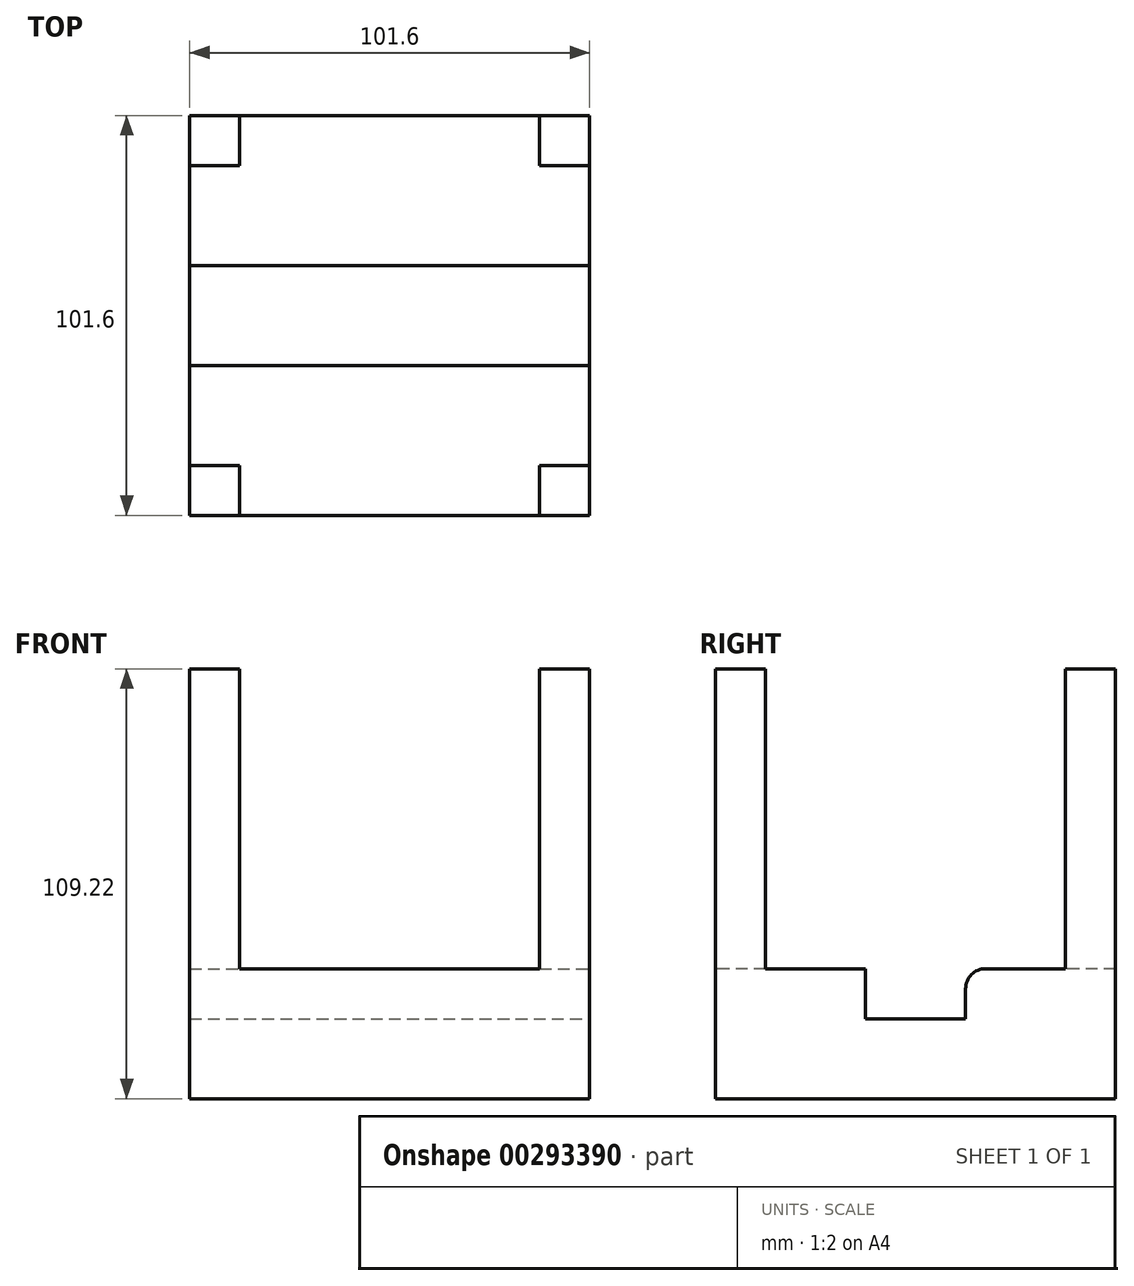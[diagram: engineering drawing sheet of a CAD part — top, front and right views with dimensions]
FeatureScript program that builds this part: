
annotation { "Feature Type Name" : "Feature", "Feature Type Description" : "" }
export const myFeature = defineFeature(function(context is Context, id is Id, definition is map)
    precondition{}
    {
        {
            var Q0;
            Q0=qCreatedBy(makeId("Top.planeOp"),FACE);
            var sketch = newSketch(context, id + "F0", { "sketchPlane" : qUnion([Q0])});
            skLineSegment(sketch, "E0.bottom", {"start": v(50.8, 50.8) * mm, "end": v(-50.8, 50.8) * mm});
            skLineSegment(sketch, "E0.top", {"start": v(50.8, -50.8) * mm, "end": v(-50.8, -50.8) * mm});
            skLineSegment(sketch, "E0.left", {"start": v(50.8, 50.8) * mm, "end": v(50.8, -50.8) * mm});
            skLineSegment(sketch, "E0.right", {"start": v(-50.8, 50.8) * mm, "end": v(-50.8, -50.8) * mm});
            skPoint(sketch, "E0.middle", {"position": v(0, 0) * mm});
            skSolve(sketch);
        }
        {
            var Q0;
            Q0=makeQuery(id+"F0.imprint","IMPRINT",FACE,{"disambiguationData":[TD([[makeQuery(id+"F0.imprint","IMPRINT",EDGE,{"derivedFrom":sQuery(id+"F0.wireOp",EDGE,"E0.bottom")}),1.0]])]});
            extrude(context, id + "F1", {"entities" : qUnion([Q0]), "depth" : 33.02 * mm});
        }
        {
            var Q0;
            Q0=makeQuery(id+"F1.opExtrude","CAP_FACE",FACE,{"disambiguationData":[OSD([sQuery(id+"F0.wireOp",EDGE,"E0.bottom"),sQuery(id+"F0.wireOp",EDGE,"E0.top"),sQuery(id+"F0.wireOp",EDGE,"E0.left"),sQuery(id+"F0.wireOp",EDGE,"E0.right")])],"isStart":false});
            var sketch = newSketch(context, id + "F2", { "sketchPlane" : qUnion([Q0])});
            skLineSegment(sketch, "E1", {"start": v(-50.8, 50.8) * mm, "end": v(-38.1, 50.8) * mm});
            skLineSegment(sketch, "E2", {"start": v(-38.1, 50.8) * mm, "end": v(-38.1, 38.1) * mm});
            skLineSegment(sketch, "E3", {"start": v(-38.1, 38.1) * mm, "end": v(-50.8, 38.1) * mm});
            skLineSegment(sketch, "E4", {"start": v(50.8, 50.8) * mm, "end": v(38.1, 50.8) * mm});
            skLineSegment(sketch, "E5", {"start": v(38.1, 50.8) * mm, "end": v(38.1, 38.1) * mm});
            skLineSegment(sketch, "E6", {"start": v(38.1, 38.1) * mm, "end": v(50.8, 38.1) * mm});
            skLineSegment(sketch, "E7", {"start": v(-50.8, -50.8) * mm, "end": v(-50.8, -38.1) * mm});
            skLineSegment(sketch, "E8", {"start": v(-50.8, -38.1) * mm, "end": v(-38.1, -38.1) * mm});
            skLineSegment(sketch, "E9", {"start": v(-38.1, -38.1) * mm, "end": v(-38.1, -50.8) * mm});
            skLineSegment(sketch, "E10", {"start": v(50.8, -50.8) * mm, "end": v(38.1, -50.8) * mm});
            skLineSegment(sketch, "E11", {"start": v(38.1, -50.8) * mm, "end": v(38.1, -38.1) * mm});
            skLineSegment(sketch, "E12", {"start": v(38.1, -38.1) * mm, "end": v(50.8, -38.1) * mm});
            skSolve(sketch);
        }
        {
            var Q0;
            {var subQ0=sQuery(id+"F2.wireOp",EDGE,"E10");Q0=makeQuery(id+"F2.imprint","IMPRINT",FACE,{"disambiguationData":[TD([[makeQuery(id+"F2.imprint","IMPRINT",EDGE,{"derivedFrom":subQ0}),-1.0]])]});}
            var Q1;
            {var subQ0=sQuery(id+"F2.wireOp",EDGE,"E7");Q1=makeQuery(id+"F2.imprint","IMPRINT",FACE,{"disambiguationData":[TD([[makeQuery(id+"F2.imprint","IMPRINT",EDGE,{"derivedFrom":subQ0}),1.0]])]});}
            var Q2;
            {var subQ0=sQuery(id+"F2.wireOp",EDGE,"E1");Q2=makeQuery(id+"F2.imprint","IMPRINT",FACE,{"disambiguationData":[TD([[makeQuery(id+"F2.imprint","IMPRINT",EDGE,{"derivedFrom":subQ0}),1.0]])]});}
            var Q3;
            {var subQ0=sQuery(id+"F2.wireOp",EDGE,"E4");Q3=makeQuery(id+"F2.imprint","IMPRINT",FACE,{"disambiguationData":[TD([[makeQuery(id+"F2.imprint","IMPRINT",EDGE,{"derivedFrom":subQ0}),1.0]])]});}
            extrude(context, id + "F3", {"entities" : qUnion([Q0, Q1, Q2, Q3]), "operationType" : NewBodyOperationType.ADD, "depth" : 76.2 * mm});
        }
        {
            var Q0;
            Q0=makeQuery(id+"F1.opExtrude","CAP_FACE",FACE,{"disambiguationData":[OSD([sQuery(id+"F0.wireOp",EDGE,"E0.bottom"),sQuery(id+"F0.wireOp",EDGE,"E0.top"),sQuery(id+"F0.wireOp",EDGE,"E0.left"),sQuery(id+"F0.wireOp",EDGE,"E0.right")])],"isStart":false});
            var sketch = newSketch(context, id + "F4", { "sketchPlane" : qUnion([Q0])});
            skLineSegment(sketch, "E13", {"start": v(-50.8, 38.1) * mm, "end": v(-50.8, 12.7) * mm});
            skLineSegment(sketch, "E14", {"start": v(-50.8, 12.7) * mm, "end": v(50.8, 12.7) * mm});
            skLineSegment(sketch, "E15", {"start": v(50.8, 12.7) * mm, "end": v(50.8, 38.1) * mm});
            skLineSegment(sketch, "E16", {"start": v(-50.8, -38.1) * mm, "end": v(-50.8, -12.7) * mm});
            skLineSegment(sketch, "E17", {"start": v(-50.8, -12.7) * mm, "end": v(50.8, -12.7) * mm});
            skSolve(sketch);
        }
        {
            var Q0;
            {var subQ0=sQuery(id+"F4.wireOp",EDGE,"E14");Q0=makeQuery(id+"F4.imprint","IMPRINT",FACE,{"disambiguationData":[TD([[makeQuery(id+"F4.imprint","IMPRINT",EDGE,{"derivedFrom":subQ0}),-1.0]])]});}
            extrude(context, id + "F5", {"entities" : qUnion([Q0]), "operationType" : NewBodyOperationType.REMOVE, "oppositeDirection" : true, "depth" : 12.7 * mm});
        }
        {
            var Q0;
            Q0=makeQuery(id+"F5.boolean.opBoolean","COPY",EDGE,{"derivedFrom":makeQuery(id+"F5.opExtrude","CAP_EDGE",EDGE,{"disambiguationData":[OSD([sQuery(id+"F4.wireOp",EDGE,"E14")])],"isStart":true})});
            var Q1;
            Q1=makeQuery(id+"F5.boolean.opBoolean","COPY",EDGE,{"derivedFrom":makeQuery(id+"F5.opExtrude","CAP_EDGE",EDGE,{"disambiguationData":[OSD([sQuery(id+"F4.wireOp",EDGE,"E17")])],"isStart":true})});
            fillet(context, id + "F6", {"entities" : qUnion([Q0, Q1]), "radius" : 5.08 * mm, "tangentPropagation" : true, "allowEdgeOverflow" : false});
        }
    });
